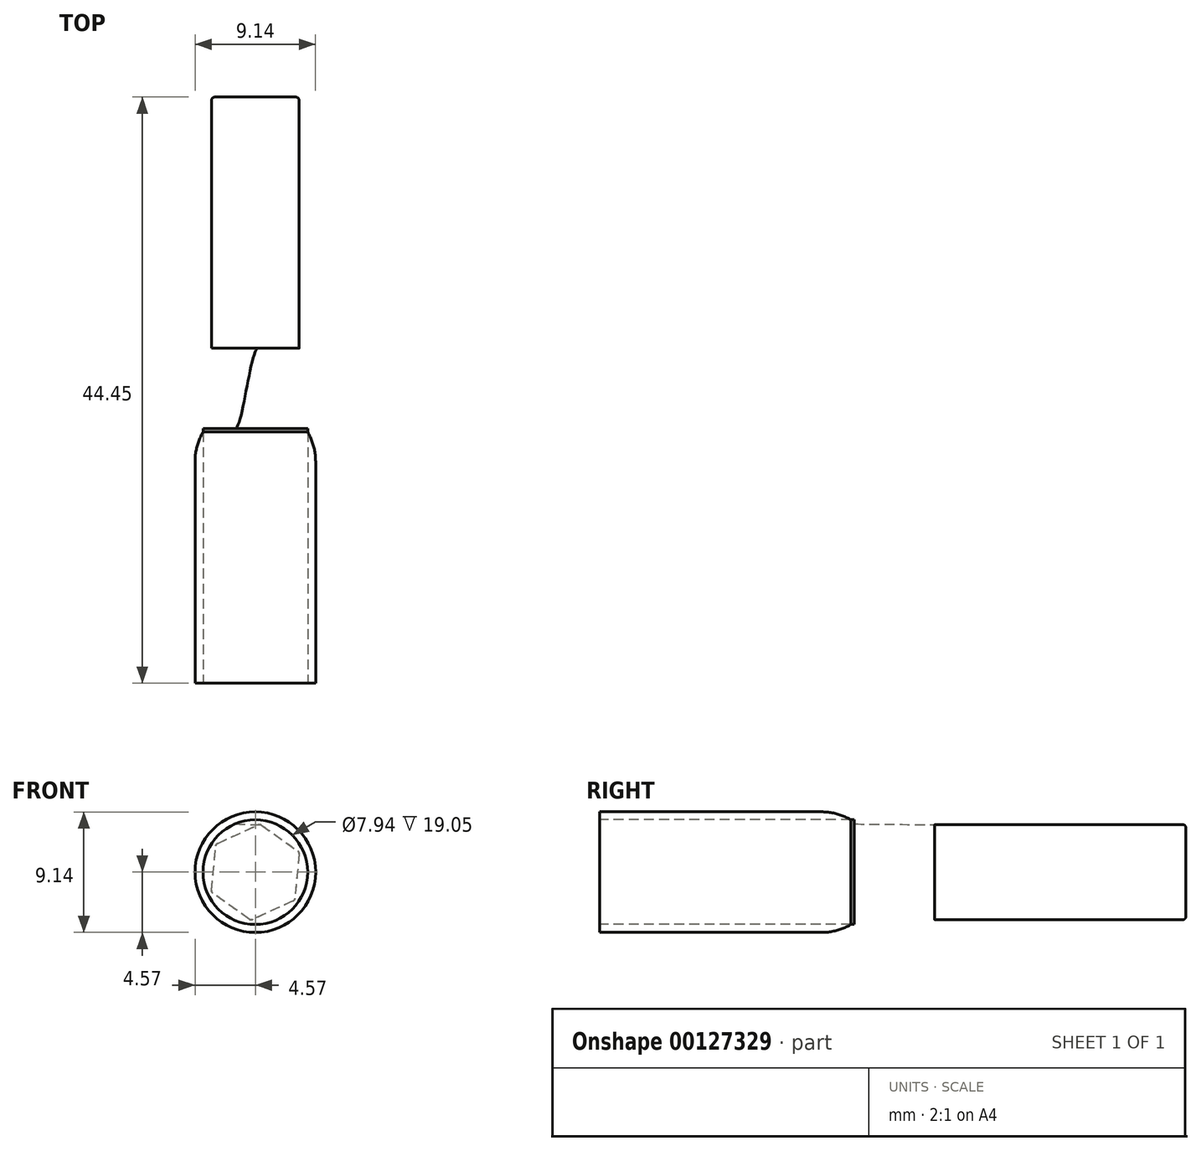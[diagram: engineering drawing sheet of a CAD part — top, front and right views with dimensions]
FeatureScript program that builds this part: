
annotation { "Feature Type Name" : "Feature", "Feature Type Description" : "" }
export const myFeature = defineFeature(function(context is Context, id is Id, definition is map)
    precondition{}
    {
        {
            var Q0;
            Q0=qCreatedBy(makeId("Front.planeOp"),FACE);
            var sketch = newSketch(context, id + "F0", { "sketchPlane" : qUnion([Q0])});
            skCircle(sketch, "E0.cCircle", {"center": v(0, 0) * mm, "radius": 3.67 * mm, "construction": true});
            skLineSegment(sketch, "E0.0", {"start": v(-3, 2.12) * mm, "end": v(0.34, 3.65) * mm});
            skLineSegment(sketch, "E0.1", {"start": v(0.34, 3.65) * mm, "end": v(3.33, 1.53) * mm});
            skLineSegment(sketch, "E0.2", {"start": v(3.33, 1.53) * mm, "end": v(3, -2.12) * mm});
            skLineSegment(sketch, "E0.3", {"start": v(3, -2.12) * mm, "end": v(-0.34, -3.65) * mm});
            skLineSegment(sketch, "E0.4", {"start": v(-0.34, -3.65) * mm, "end": v(-3.33, -1.53) * mm});
            skLineSegment(sketch, "E0.5", {"start": v(-3.33, -1.53) * mm, "end": v(-3, 2.12) * mm});
            skSolve(sketch);
        }
        {
            var Q0;
            Q0=makeQuery(id+"F0.imprint","IMPRINT",FACE,{"disambiguationData":[TD([[makeQuery(id+"F0.imprint","IMPRINT",EDGE,{"derivedFrom":sQuery(id+"F0.wireOp",EDGE,"E0.0")}),-1.0]])]});
            extrude(context, id + "F1", {"entities" : qUnion([Q0]), "oppositeDirection" : true, "depth" : 44.45 * mm, "hasSecondDirection" : true, "secondDirectionOppositeDirection" : true, "secondDirectionDepth" : 25.4 * mm});
        }
        {
            var Q0;
            Q0=makeQuery(id+"F1.opExtrude","CAP_EDGE",EDGE,{"disambiguationData":[OSD([sQuery(id+"F0.wireOp",EDGE,"E0.2")])],"isStart":false});
            var Q1;
            Q1=makeQuery(id+"F1.opExtrude","CAP_EDGE",EDGE,{"disambiguationData":[OSD([sQuery(id+"F0.wireOp",EDGE,"E0.3")])],"isStart":false});
            var Q2;
            Q2=makeQuery(id+"F1.opExtrude","CAP_EDGE",EDGE,{"disambiguationData":[OSD([sQuery(id+"F0.wireOp",EDGE,"E0.4")])],"isStart":false});
            var Q3;
            Q3=makeQuery(id+"F1.opExtrude","CAP_EDGE",EDGE,{"disambiguationData":[OSD([sQuery(id+"F0.wireOp",EDGE,"E0.5")])],"isStart":false});
            var Q4;
            Q4=makeQuery(id+"F1.opExtrude","CAP_EDGE",EDGE,{"disambiguationData":[OSD([sQuery(id+"F0.wireOp",EDGE,"E0.0")])],"isStart":false});
            var Q5;
            Q5=makeQuery(id+"F1.opExtrude","CAP_EDGE",EDGE,{"disambiguationData":[OSD([sQuery(id+"F0.wireOp",EDGE,"E0.1")])],"isStart":false});
            var Q6;
            Q6=makeQuery(id+"F1.opExtrude","SWEPT_EDGE",EDGE,{"disambiguationData":[OSD([sQuery(id+"F0.wireOp",EDGE,"E0.1"),sQuery(id+"F0.wireOp",EDGE,"E0.2")])]});
            var Q7;
            Q7=makeQuery(id+"F1.opExtrude","SWEPT_EDGE",EDGE,{"disambiguationData":[OSD([sQuery(id+"F0.wireOp",EDGE,"E0.2"),sQuery(id+"F0.wireOp",EDGE,"E0.3")])]});
            var Q8;
            Q8=makeQuery(id+"F1.opExtrude","SWEPT_EDGE",EDGE,{"disambiguationData":[OSD([sQuery(id+"F0.wireOp",EDGE,"E0.0"),sQuery(id+"F0.wireOp",EDGE,"E0.1")])]});
            var Q9;
            Q9=makeQuery(id+"F1.opExtrude","SWEPT_EDGE",EDGE,{"disambiguationData":[OSD([sQuery(id+"F0.wireOp",EDGE,"E0.0"),sQuery(id+"F0.wireOp",EDGE,"E0.5")])]});
            var Q10;
            Q10=makeQuery(id+"F1.opExtrude","SWEPT_EDGE",EDGE,{"disambiguationData":[OSD([sQuery(id+"F0.wireOp",EDGE,"E0.4"),sQuery(id+"F0.wireOp",EDGE,"E0.5")])]});
            var Q11;
            Q11=makeQuery(id+"F1.opExtrude","SWEPT_EDGE",EDGE,{"disambiguationData":[OSD([sQuery(id+"F0.wireOp",EDGE,"E0.3"),sQuery(id+"F0.wireOp",EDGE,"E0.4")])]});
            fillet(context, id + "F2", {"entities" : qUnion([Q0, Q1, Q2, Q3, Q4, Q5, Q6, Q7, Q8, Q9, Q10, Q11]), "radius" : 0.25 * mm, "tangentPropagation" : true, "allowEdgeOverflow" : false});
        }
        {
            var Q0;
            Q0=qCreatedBy(makeId("Front.planeOp"),FACE);
            var sketch = newSketch(context, id + "F3", { "sketchPlane" : qUnion([Q0])});
            skCircle(sketch, "E1", {"center": v(0, 0) * mm, "radius": 3.97 * mm});
            skCircle(sketch, "E2", {"center": v(0, 0) * mm, "radius": 4.57 * mm});
            skSolve(sketch);
        }
        {
            var Q0;
            Q0 = qSketchRegion(id + "F3", true);
            extrude(context, id + "F4", {"entities" : qUnion([Q0]), "oppositeDirection" : true, "depth" : 19.05 * mm});
        }
        {
            var Q0;
            Q0=makeQuery(id+"F4.opExtrude","CAP_FACE",FACE,{"disambiguationData":[OSD([sQuery(id+"F3.wireOp",EDGE,"E1"),sQuery(id+"F3.wireOp",EDGE,"E2")])],"isStart":false});
            var sketch = newSketch(context, id + "F5", { "sketchPlane" : qUnion([Q0])});
            skSolve(sketch);
        }
        {
            var Q0;
            Q0=makeQuery(id+"F5.imprint","IMPRINT",FACE,{"disambiguationData":[TD([[makeQuery(id+"F5.imprint","IMPRINT",EDGE,{"derivedFrom":makeQuery(id+"F4.opExtrude","CAP_EDGE",EDGE,{"disambiguationData":[OSD([sQuery(id+"F3.wireOp",EDGE,"E1")])],"isStart":false})}),-1.0]])]});
            extrude(context, id + "F6", {"entities" : qUnion([Q0]), "operationType" : NewBodyOperationType.ADD, "depth" : 0.25 * mm});
        }
        {
            var Q1;
            Q1=makeQuery(id+"F6.opExtrude","CAP_FACE",FACE,{"disambiguationData":[OSD([sQuery(id+"F3.wireOp",EDGE,"E1")])],"isStart":false});
            var Q2;
            Q2=makeQuery(id+"F1.opExtrude","CAP_FACE",FACE,{"disambiguationData":[OSD([sQuery(id+"F0.wireOp",EDGE,"E0.0"),sQuery(id+"F0.wireOp",EDGE,"E0.1"),sQuery(id+"F0.wireOp",EDGE,"E0.2"),sQuery(id+"F0.wireOp",EDGE,"E0.3"),sQuery(id+"F0.wireOp",EDGE,"E0.4"),sQuery(id+"F0.wireOp",EDGE,"E0.5")])],"isStart":true});
            loft(context, id + "F7", {"operationType" : NewBodyOperationType.ADD, "startCondition" : LoftEndDerivativeType.TANGENT_TO_PROFILE, "startMagnitude" : 1, "endCondition" : LoftEndDerivativeType.TANGENT_TO_PROFILE, "endMagnitude" : 1, "sheetProfilesArray" : [{ "sheetProfileEntities" : qUnion([Q1]) }, { "sheetProfileEntities" : qUnion([Q2]) }]});
        }
        {
            var Q0;
            Q0=makeQuery(id+"F4.opExtrude","CAP_EDGE",EDGE,{"disambiguationData":[OSD([sQuery(id+"F3.wireOp",EDGE,"E2")])],"isStart":false});
            fillet(context, id + "F8", {"entities" : qUnion([Q0]), "radius" : 4.42 * mm, "tangentPropagation" : true, "allowEdgeOverflow" : false});
        }
    });
